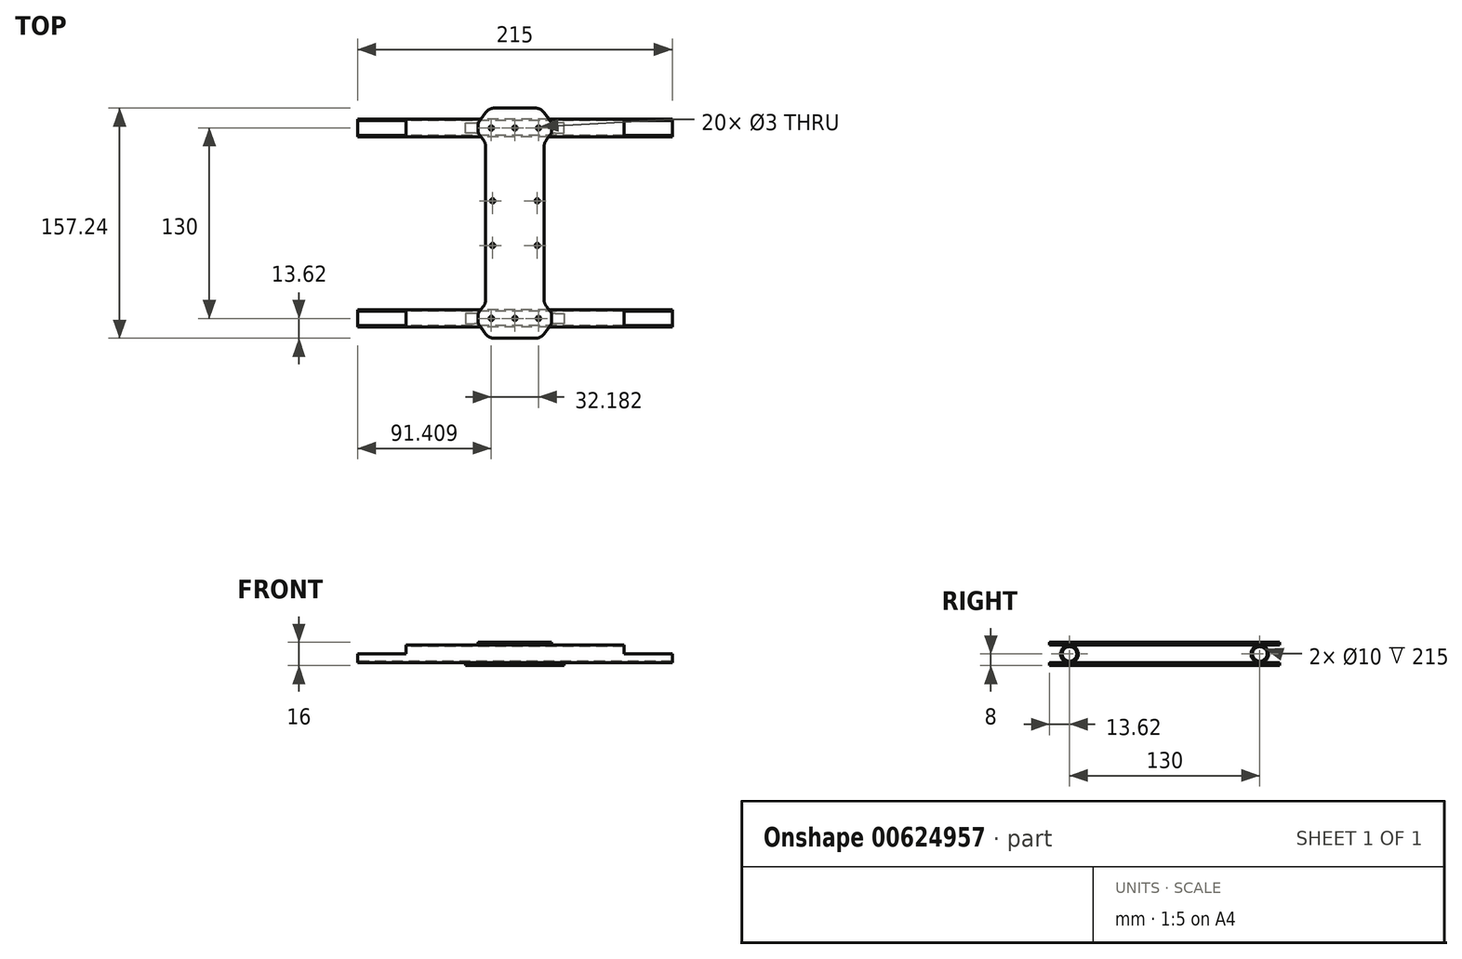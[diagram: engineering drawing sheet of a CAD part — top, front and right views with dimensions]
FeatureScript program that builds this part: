
annotation { "Feature Type Name" : "Feature", "Feature Type Description" : "" }
export const myFeature = defineFeature(function(context is Context, id is Id, definition is map)
    precondition{}
    {
        {
            var Q0;
            Q0=qCreatedBy(makeId("Top.planeOp"),FACE);
            var sketch = newSketch(context, id + "F0", { "sketchPlane" : qUnion([Q0])});
            skLineSegment(sketch, "E0.bottom", {"start": v(-20, 65) * mm, "end": v(20, 65) * mm, "construction": true});
            skLineSegment(sketch, "E0.top", {"start": v(-20, -65) * mm, "end": v(20, -65) * mm, "construction": true});
            skLineSegment(sketch, "E0.left", {"start": v(-20, 65) * mm, "end": v(-20, -65) * mm, "construction": true});
            skLineSegment(sketch, "E0.right", {"start": v(20, 65) * mm, "end": v(20, -65) * mm, "construction": true});
            skPoint(sketch, "E0.middle", {"position": v(0, 0) * mm});
            skSolve(sketch);
        }
        {
            var Q0;
            Q0=qCreatedBy(makeId("Right.planeOp"),FACE);
            var sketch = newSketch(context, id + "F1", { "sketchPlane" : qUnion([Q0])});
            skCircle(sketch, "E1", {"center": v(-65, 0) * mm, "radius": 6 * mm});
            skLineSegment(sketch, "E2", {"start": v(-65, 0) * mm, "end": v(0, 0) * mm, "construction": true});
            skLineSegment(sketch, "E3", {"start": v(0, 0) * mm, "end": v(64.7, 0) * mm, "construction": true});
            skLineSegment(sketch, "E4", {"start": v(0, 0) * mm, "end": v(0, 7.86) * mm, "construction": true});
            skCircle(sketch, "E5.MirrorC", {"center": v(65, 0) * mm, "radius": 6 * mm});
            skCircle(sketch, "E6", {"center": v(-65, 0) * mm, "radius": 5 * mm});
            skCircle(sketch, "E7.MirrorC", {"center": v(65, 0) * mm, "radius": 5 * mm});
            skSolve(sketch);
        }
        {
            var Q0;
            Q0 = qSketchRegion(id + "F1", true);
            extrude(context, id + "F2", {"entities" : qUnion([Q0]), "endBound" : BoundingType.SYMMETRIC, "depth" : 215 * mm, "offsetDistance" : 25 * mm});
        }
        {
            var Q0;
            Q0=qCreatedBy(makeId("Top.planeOp"),FACE);
            var sketch = newSketch(context, id + "F3", { "sketchPlane" : qUnion([Q0])});
            skLineSegment(sketch, "E8", {"start": v(-20, -54.92) * mm, "end": v(-25.19, -61.5) * mm});
            skLineSegment(sketch, "E9", {"start": v(-25.19, -61.5) * mm, "end": v(-33.69, -61.5) * mm});
            skLineSegment(sketch, "E10", {"start": v(-33.69, -61.5) * mm, "end": v(-33.62, -68.5) * mm});
            skLineSegment(sketch, "E11", {"start": v(-33.62, -68.5) * mm, "end": v(-25.12, -68.5) * mm});
            skLineSegment(sketch, "E12", {"start": v(-20, -54.92) * mm, "end": v(-20, 0) * mm});
            skLineSegment(sketch, "E13", {"start": v(-20, 0) * mm, "end": v(0, 0) * mm, "construction": true});
            skLineSegment(sketch, "E14", {"start": v(0, -75.74) * mm, "end": v(0, 0) * mm, "construction": true});
            skLineSegment(sketch, "E15", {"start": v(-25.12, -68.5) * mm, "end": v(-17.75, -78.62) * mm});
            skLineSegment(sketch, "E16", {"start": v(-17.75, -78.62) * mm, "end": v(0, -78.62) * mm});
            skLineSegment(sketch, "E17.MirrorCS", {"start": v(25.12, -68.5) * mm, "end": v(17.75, -78.62) * mm});
            skLineSegment(sketch, "E18.MirrorCS", {"start": v(25.19, -61.5) * mm, "end": v(33.69, -61.5) * mm});
            skLineSegment(sketch, "E19.MirrorCS", {"start": v(33.69, -61.5) * mm, "end": v(33.62, -68.5) * mm});
            skLineSegment(sketch, "E20.MirrorCS", {"start": v(20, 0) * mm, "end": v(0, 0) * mm, "construction": true});
            skLineSegment(sketch, "E21.MirrorCS", {"start": v(20, -54.92) * mm, "end": v(25.19, -61.5) * mm});
            skLineSegment(sketch, "E22.MirrorCS", {"start": v(20, -54.92) * mm, "end": v(20, 0) * mm});
            skLineSegment(sketch, "E23.MirrorCS", {"start": v(17.75, -78.62) * mm, "end": v(0, -78.62) * mm});
            skLineSegment(sketch, "E24.MirrorCS", {"start": v(33.62, -68.5) * mm, "end": v(25.12, -68.5) * mm});
            skLineSegment(sketch, "E25.MirrorCS", {"start": v(33.69, 61.5) * mm, "end": v(33.62, 68.5) * mm});
            skLineSegment(sketch, "E26.MirrorCS", {"start": v(-33.62, 68.5) * mm, "end": v(-25.12, 68.5) * mm});
            skLineSegment(sketch, "E27.MirrorCS", {"start": v(-33.69, 61.5) * mm, "end": v(-33.62, 68.5) * mm});
            skLineSegment(sketch, "E28.MirrorCS", {"start": v(17.75, 78.62) * mm, "end": v(0, 78.62) * mm});
            skLineSegment(sketch, "E29.MirrorCS", {"start": v(-20, 54.92) * mm, "end": v(-20, 0) * mm});
            skLineSegment(sketch, "E30.MirrorCS", {"start": v(-20, 54.92) * mm, "end": v(-25.19, 61.5) * mm});
            skLineSegment(sketch, "E31.MirrorCS", {"start": v(-17.75, 78.62) * mm, "end": v(0, 78.62) * mm});
            skLineSegment(sketch, "E32.MirrorCS", {"start": v(20, 54.92) * mm, "end": v(20, 0) * mm});
            skLineSegment(sketch, "E33.MirrorCS", {"start": v(-25.19, 61.5) * mm, "end": v(-33.69, 61.5) * mm});
            skLineSegment(sketch, "E34.MirrorCS", {"start": v(25.12, 68.5) * mm, "end": v(17.75, 78.62) * mm});
            skLineSegment(sketch, "E35.MirrorCS", {"start": v(20, 54.92) * mm, "end": v(25.19, 61.5) * mm});
            skLineSegment(sketch, "E36.MirrorCS", {"start": v(25.19, 61.5) * mm, "end": v(33.69, 61.5) * mm});
            skLineSegment(sketch, "E37.MirrorCS", {"start": v(-25.12, 68.5) * mm, "end": v(-17.75, 78.62) * mm});
            skLineSegment(sketch, "E38.MirrorCS", {"start": v(33.62, 68.5) * mm, "end": v(25.12, 68.5) * mm});
            skLineSegment(sketch, "E39.MirrorCS", {"start": v(0, 75.74) * mm, "end": v(0, 0) * mm, "construction": true});
            skLineSegment(sketch, "E40", {"start": v(0, -65) * mm, "end": v(-33.65, -65) * mm, "construction": true});
            skCircle(sketch, "E41", {"center": v(-16.1, -65) * mm, "radius": 1.5 * mm});
            skCircle(sketch, "E42.MirrorC", {"center": v(16.1, -65) * mm, "radius": 1.5 * mm});
            skCircle(sketch, "E43.MirrorC", {"center": v(16.1, 65) * mm, "radius": 1.5 * mm});
            skCircle(sketch, "E44.MirrorC", {"center": v(-16.1, 65) * mm, "radius": 1.5 * mm});
            skCircle(sketch, "E45", {"center": v(0, -65) * mm, "radius": 1.5 * mm});
            skCircle(sketch, "E46.MirrorC", {"center": v(0, 65) * mm, "radius": 1.5 * mm});
            skPoint(sketch, "E47.middle", {"position": v(0, 0) * mm});
            skCircle(sketch, "E48", {"center": v(-15.25, 15.25) * mm, "radius": 1.5 * mm});
            skCircle(sketch, "E49.MirrorC", {"center": v(-15.25, -15.25) * mm, "radius": 1.5 * mm});
            skCircle(sketch, "E50.MirrorC", {"center": v(15.25, 15.25) * mm, "radius": 1.5 * mm});
            skCircle(sketch, "E51.MirrorC", {"center": v(15.25, -15.25) * mm, "radius": 1.5 * mm});
            skSolve(sketch);
        }
        {
            var Q0;
            Q0=makeQuery(id+"F3.imprint","IMPRINT",FACE,{"disambiguationData":[TD([[makeQuery(id+"F3.imprint","IMPRINT",EDGE,{"derivedFrom":sQuery(id+"F3.wireOp",EDGE,"E8")}),1.0]])]});
            extrude(context, id + "F4", {"entities" : qUnion([Q0]), "oppositeDirection" : true, "depth" : 8 * mm, "offsetDistance" : 25 * mm, "hasSecondDirection" : true, "secondDirectionOppositeDirection" : true, "secondDirectionDepth" : 6 * mm});
        }
        {
            var Q0;
            Q0=qCreatedBy(makeId("Top.planeOp"),FACE);
            var sketch = newSketch(context, id + "F5", { "sketchPlane" : qUnion([Q0])});
            skLineSegment(sketch, "E52", {"start": v(-20, -54.92) * mm, "end": v(-25.19, -61.5) * mm});
            skLineSegment(sketch, "E53", {"start": v(-20, -54.92) * mm, "end": v(-20, 0) * mm});
            skLineSegment(sketch, "E54", {"start": v(-20, 0) * mm, "end": v(0, 0) * mm, "construction": true});
            skLineSegment(sketch, "E55", {"start": v(0, -75.74) * mm, "end": v(0, 0) * mm, "construction": true});
            skLineSegment(sketch, "E56", {"start": v(-25.12, -68.5) * mm, "end": v(-17.75, -78.62) * mm});
            skLineSegment(sketch, "E57", {"start": v(-17.75, -78.62) * mm, "end": v(0, -78.62) * mm});
            skLineSegment(sketch, "E58.MirrorCS", {"start": v(25.12, -68.5) * mm, "end": v(17.75, -78.62) * mm});
            skLineSegment(sketch, "E59.MirrorCS", {"start": v(20, 0) * mm, "end": v(0, 0) * mm, "construction": true});
            skLineSegment(sketch, "E60.MirrorCS", {"start": v(20, -54.92) * mm, "end": v(25.19, -61.5) * mm});
            skLineSegment(sketch, "E61.MirrorCS", {"start": v(20, -54.92) * mm, "end": v(20, 0) * mm});
            skLineSegment(sketch, "E62.MirrorCS", {"start": v(17.75, -78.62) * mm, "end": v(0, -78.62) * mm});
            skLineSegment(sketch, "E63.MirrorCS", {"start": v(17.75, 78.62) * mm, "end": v(0, 78.62) * mm});
            skLineSegment(sketch, "E64.MirrorCS", {"start": v(-20, 54.92) * mm, "end": v(-20, 0) * mm});
            skLineSegment(sketch, "E65.MirrorCS", {"start": v(-20, 54.92) * mm, "end": v(-25.19, 61.5) * mm});
            skLineSegment(sketch, "E66.MirrorCS", {"start": v(-17.75, 78.62) * mm, "end": v(0, 78.62) * mm});
            skLineSegment(sketch, "E67.MirrorCS", {"start": v(20, 54.92) * mm, "end": v(20, 0) * mm});
            skLineSegment(sketch, "E68.MirrorCS", {"start": v(25.12, 68.5) * mm, "end": v(17.75, 78.62) * mm});
            skLineSegment(sketch, "E69.MirrorCS", {"start": v(20, 54.92) * mm, "end": v(25.19, 61.5) * mm});
            skLineSegment(sketch, "E70.MirrorCS", {"start": v(-25.12, 68.5) * mm, "end": v(-17.75, 78.62) * mm});
            skLineSegment(sketch, "E71.MirrorCS", {"start": v(0, 75.74) * mm, "end": v(0, 0) * mm, "construction": true});
            skCircle(sketch, "E72", {"center": v(-16.1, -65) * mm, "radius": 1.5 * mm});
            skCircle(sketch, "E73.MirrorC", {"center": v(16.1, -65) * mm, "radius": 1.5 * mm});
            skCircle(sketch, "E74.MirrorC", {"center": v(16.1, 65) * mm, "radius": 1.5 * mm});
            skCircle(sketch, "E75.MirrorC", {"center": v(-16.1, 65) * mm, "radius": 1.5 * mm});
            skCircle(sketch, "E76", {"center": v(0, -65) * mm, "radius": 1.5 * mm});
            skCircle(sketch, "E77.MirrorC", {"center": v(0, 65) * mm, "radius": 1.5 * mm});
            skLineSegment(sketch, "E78", {"start": v(25.12, -68.5) * mm, "end": v(25.19, -61.5) * mm});
            skLineSegment(sketch, "E79.MirrorCS", {"start": v(-25.12, -68.5) * mm, "end": v(-25.19, -61.5) * mm});
            skLineSegment(sketch, "E80", {"start": v(25.19, 61.5) * mm, "end": v(25.12, 68.5) * mm});
            skLineSegment(sketch, "E81", {"start": v(-25.19, 61.5) * mm, "end": v(-25.12, 68.5) * mm});
            skPoint(sketch, "E82.middle", {"position": v(0, 0) * mm});
            skCircle(sketch, "E83", {"center": v(-15.25, 15.25) * mm, "radius": 1.5 * mm});
            skCircle(sketch, "E84.MirrorC", {"center": v(15.25, 15.25) * mm, "radius": 1.5 * mm});
            skCircle(sketch, "E85.MirrorC", {"center": v(15.25, -15.25) * mm, "radius": 1.5 * mm});
            skCircle(sketch, "E86.MirrorC", {"center": v(-15.25, -15.25) * mm, "radius": 1.5 * mm});
            skSolve(sketch);
        }
        {
            var Q0;
            Q0 = qSketchRegion(id + "F5", true);
            extrude(context, id + "F6", {"entities" : qUnion([Q0]), "depth" : 8 * mm, "offsetDistance" : 25 * mm, "hasSecondDirection" : true, "secondDirectionOppositeDirection" : false, "secondDirectionDepth" : 6 * mm});
        }
        {
            var Q0;
            Q0=qCreatedBy(makeId("Top.planeOp"),FACE);
            var sketch = newSketch(context, id + "F7", { "sketchPlane" : qUnion([Q0])});
            skLineSegment(sketch, "E87", {"start": v(0, 0) * mm, "end": v(0, -65) * mm, "construction": true});
            skLineSegment(sketch, "E88", {"start": v(0, -65) * mm, "end": v(91, -65) * mm, "construction": true});
            skLineSegment(sketch, "E89", {"start": v(0, 0) * mm, "end": v(43.65, 0) * mm, "construction": true});
            skLineSegment(sketch, "E90.bottom", {"start": v(74.5, -59) * mm, "end": v(107.5, -59) * mm});
            skLineSegment(sketch, "E90.top", {"start": v(74.5, -71) * mm, "end": v(107.5, -71) * mm});
            skLineSegment(sketch, "E90.left", {"start": v(74.5, -59) * mm, "end": v(74.5, -71) * mm});
            skLineSegment(sketch, "E90.right", {"start": v(107.5, -59) * mm, "end": v(107.5, -71) * mm});
            skPoint(sketch, "E90.middle", {"position": v(91, -65) * mm});
            skLineSegment(sketch, "E91.MirrorCS", {"start": v(-74.5, -59) * mm, "end": v(-107.5, -59) * mm});
            skLineSegment(sketch, "E92.MirrorCS", {"start": v(-74.5, -59) * mm, "end": v(-74.5, -71) * mm});
            skLineSegment(sketch, "E93.MirrorCS", {"start": v(-74.5, -71) * mm, "end": v(-107.5, -71) * mm});
            skLineSegment(sketch, "E94.MirrorCS", {"start": v(-107.5, -59) * mm, "end": v(-107.5, -71) * mm});
            skPoint(sketch, "E95.MirrorP", {"position": v(-91, -65) * mm});
            skLineSegment(sketch, "E96.MirrorCS", {"start": v(107.5, 59) * mm, "end": v(107.5, 71) * mm});
            skLineSegment(sketch, "E97.MirrorCS", {"start": v(0, 65) * mm, "end": v(91, 65) * mm, "construction": true});
            skLineSegment(sketch, "E98.MirrorCS", {"start": v(-74.5, 59) * mm, "end": v(-74.5, 71) * mm});
            skLineSegment(sketch, "E99.MirrorCS", {"start": v(-107.5, 59) * mm, "end": v(-107.5, 71) * mm});
            skPoint(sketch, "E100.MirrorP", {"position": v(91, 65) * mm});
            skLineSegment(sketch, "E101.MirrorCS", {"start": v(-74.5, 59) * mm, "end": v(-107.5, 59) * mm});
            skPoint(sketch, "E102.MirrorP", {"position": v(-91, 65) * mm});
            skLineSegment(sketch, "E103.MirrorCS", {"start": v(74.5, 59) * mm, "end": v(74.5, 71) * mm});
            skLineSegment(sketch, "E104.MirrorCS", {"start": v(0, 0) * mm, "end": v(0, 65) * mm, "construction": true});
            skLineSegment(sketch, "E105.MirrorCS", {"start": v(-74.5, 71) * mm, "end": v(-107.5, 71) * mm});
            skLineSegment(sketch, "E106.MirrorCS", {"start": v(74.5, 71) * mm, "end": v(107.5, 71) * mm});
            skLineSegment(sketch, "E107.MirrorCS", {"start": v(74.5, 59) * mm, "end": v(107.5, 59) * mm});
            skSolve(sketch);
        }
        {
            var Q0;
            Q0 = qSketchRegion(id + "F7", true);
            extrude(context, id + "F8", {"entities" : qUnion([Q0]), "operationType" : NewBodyOperationType.REMOVE, "depth" : 6 * mm, "offsetDistance" : 25 * mm});
        }
        {
            var Q0;
            Q0=makeQuery(id+"F4.opExtrude","SWEPT_EDGE",EDGE,{"disambiguationData":[OSD([sQuery(id+"F3.wireOp",EDGE,"E11"),sQuery(id+"F3.wireOp",EDGE,"E15")])]});
            var Q1;
            Q1=makeQuery(id+"F4.opExtrude","SWEPT_EDGE",EDGE,{"disambiguationData":[OSD([sQuery(id+"F3.wireOp",EDGE,"E17.MirrorCS"),sQuery(id+"F3.wireOp",EDGE,"E24.MirrorCS")])]});
            var Q2;
            Q2=makeQuery(id+"F4.opExtrude","SWEPT_EDGE",EDGE,{"disambiguationData":[OSD([sQuery(id+"F3.wireOp",EDGE,"E18.MirrorCS"),sQuery(id+"F3.wireOp",EDGE,"E21.MirrorCS")])]});
            var Q3;
            Q3=makeQuery(id+"F4.opExtrude","SWEPT_EDGE",EDGE,{"disambiguationData":[OSD([sQuery(id+"F3.wireOp",EDGE,"E8"),sQuery(id+"F3.wireOp",EDGE,"E9")])]});
            var Q4;
            Q4=makeQuery(id+"F4.opExtrude","SWEPT_EDGE",EDGE,{"disambiguationData":[OSD([sQuery(id+"F3.wireOp",EDGE,"E26.MirrorCS"),sQuery(id+"F3.wireOp",EDGE,"E37.MirrorCS")])]});
            var Q5;
            Q5=makeQuery(id+"F4.opExtrude","SWEPT_EDGE",EDGE,{"disambiguationData":[OSD([sQuery(id+"F3.wireOp",EDGE,"E34.MirrorCS"),sQuery(id+"F3.wireOp",EDGE,"E38.MirrorCS")])]});
            var Q6;
            Q6=makeQuery(id+"F4.opExtrude","SWEPT_EDGE",EDGE,{"disambiguationData":[OSD([sQuery(id+"F3.wireOp",EDGE,"E35.MirrorCS"),sQuery(id+"F3.wireOp",EDGE,"E36.MirrorCS")])]});
            var Q7;
            Q7=makeQuery(id+"F4.opExtrude","SWEPT_EDGE",EDGE,{"disambiguationData":[OSD([sQuery(id+"F3.wireOp",EDGE,"E30.MirrorCS"),sQuery(id+"F3.wireOp",EDGE,"E33.MirrorCS")])]});
            var Q8;
            Q8=makeQuery(id+"F6.opExtrude","SWEPT_EDGE",EDGE,{"disambiguationData":[OSD([sQuery(id+"F5.wireOp",EDGE,"E70.MirrorCS"),sQuery(id+"F5.wireOp",EDGE,"E81")])]});
            var Q9;
            Q9=makeQuery(id+"F6.opExtrude","SWEPT_EDGE",EDGE,{"disambiguationData":[OSD([sQuery(id+"F5.wireOp",EDGE,"E65.MirrorCS"),sQuery(id+"F5.wireOp",EDGE,"E81")])]});
            var Q10;
            Q10=makeQuery(id+"F6.opExtrude","SWEPT_EDGE",EDGE,{"disambiguationData":[OSD([sQuery(id+"F5.wireOp",EDGE,"E68.MirrorCS"),sQuery(id+"F5.wireOp",EDGE,"E80")])]});
            var Q11;
            Q11=makeQuery(id+"F6.opExtrude","SWEPT_EDGE",EDGE,{"disambiguationData":[OSD([sQuery(id+"F5.wireOp",EDGE,"E69.MirrorCS"),sQuery(id+"F5.wireOp",EDGE,"E80")])]});
            var Q12;
            Q12=makeQuery(id+"F6.opExtrude","SWEPT_EDGE",EDGE,{"disambiguationData":[OSD([sQuery(id+"F5.wireOp",EDGE,"E58.MirrorCS"),sQuery(id+"F5.wireOp",EDGE,"E78")])]});
            var Q13;
            Q13=makeQuery(id+"F6.opExtrude","SWEPT_EDGE",EDGE,{"disambiguationData":[OSD([sQuery(id+"F5.wireOp",EDGE,"E60.MirrorCS"),sQuery(id+"F5.wireOp",EDGE,"E78")])]});
            var Q14;
            Q14=makeQuery(id+"F6.opExtrude","SWEPT_EDGE",EDGE,{"disambiguationData":[OSD([sQuery(id+"F5.wireOp",EDGE,"E52"),sQuery(id+"F5.wireOp",EDGE,"E79.MirrorCS")])]});
            var Q15;
            Q15=makeQuery(id+"F6.opExtrude","SWEPT_EDGE",EDGE,{"disambiguationData":[OSD([sQuery(id+"F5.wireOp",EDGE,"E56"),sQuery(id+"F5.wireOp",EDGE,"E79.MirrorCS")])]});
            var Q16;
            Q16=makeQuery(id+"FRUV5qcOZJ5jhgf_4.opExtrude","SWEPT_EDGE",EDGE,{"disambiguationData":[OSD([sQuery(id+"FPOVCmEpiKDNWGi_4.wireOp",EDGE,"b42ecf09-6dc6-4207-b51f-dcecceab576b.MirrorCS"),sQuery(id+"FPOVCmEpiKDNWGi_4.wireOp",EDGE,"35af5927-bb7d-4a19-8fb0-2eac8ffebaeb")])]});
            var Q17;
            Q17=makeQuery(id+"FRUV5qcOZJ5jhgf_4.opExtrude","SWEPT_EDGE",EDGE,{"disambiguationData":[OSD([sQuery(id+"FPOVCmEpiKDNWGi_4.wireOp",EDGE,"97de2fec-c19a-4408-b6b3-02fe6345d77e.MirrorCS"),sQuery(id+"FPOVCmEpiKDNWGi_4.wireOp",EDGE,"35af5927-bb7d-4a19-8fb0-2eac8ffebaeb")])]});
            var Q18;
            Q18=makeQuery(id+"FRUV5qcOZJ5jhgf_4.opExtrude","SWEPT_EDGE",EDGE,{"disambiguationData":[OSD([sQuery(id+"FPOVCmEpiKDNWGi_4.wireOp",EDGE,"46e9c258-9e58-4d26-8021-a2ccb4e2b974.MirrorCS"),sQuery(id+"FPOVCmEpiKDNWGi_4.wireOp",EDGE,"e85c2889-23f9-49fd-8fc6-b68ef9be6dd2")])]});
            var Q19;
            Q19=makeQuery(id+"FRUV5qcOZJ5jhgf_4.opExtrude","SWEPT_EDGE",EDGE,{"disambiguationData":[OSD([sQuery(id+"FPOVCmEpiKDNWGi_4.wireOp",EDGE,"b1dd11ee-b3e0-4977-90c2-f60ee6d27586.MirrorCS"),sQuery(id+"FPOVCmEpiKDNWGi_4.wireOp",EDGE,"e85c2889-23f9-49fd-8fc6-b68ef9be6dd2")])]});
            var Q20;
            Q20=makeQuery(id+"FRUV5qcOZJ5jhgf_4.opExtrude","SWEPT_EDGE",EDGE,{"disambiguationData":[OSD([sQuery(id+"FPOVCmEpiKDNWGi_4.wireOp",EDGE,"41c56124-091f-4bfc-87e4-0effb01823fb.MirrorCS"),sQuery(id+"FPOVCmEpiKDNWGi_4.wireOp",EDGE,"41155186-b6f0-42d8-86f9-b8dc6bf684e1")])]});
            var Q21;
            Q21=makeQuery(id+"FRUV5qcOZJ5jhgf_4.opExtrude","SWEPT_EDGE",EDGE,{"disambiguationData":[OSD([sQuery(id+"FPOVCmEpiKDNWGi_4.wireOp",EDGE,"9b6425d3-5aca-4adc-8dc5-8d42905c519e.MirrorCS"),sQuery(id+"FPOVCmEpiKDNWGi_4.wireOp",EDGE,"41155186-b6f0-42d8-86f9-b8dc6bf684e1")])]});
            var Q22;
            Q22=makeQuery(id+"FRUV5qcOZJ5jhgf_4.opExtrude","SWEPT_EDGE",EDGE,{"disambiguationData":[OSD([sQuery(id+"FPOVCmEpiKDNWGi_4.wireOp",EDGE,"9a405053-cc7c-4e3b-ba71-51e772f208f1"),sQuery(id+"FPOVCmEpiKDNWGi_4.wireOp",EDGE,"5861f194-80c3-4196-93a7-092f7c520be6.MirrorCS")])]});
            fillet(context, id + "F9", {"entities" : qUnion([Q0, Q1, Q2, Q3, Q4, Q5, Q6, Q7, Q8, Q9, Q10, Q11, Q12, Q13, Q14, Q15, Q16, Q17, Q18, Q19, Q20, Q21, Q22]), "radius" : 5 * mm, "tangentPropagation" : true, "allowEdgeOverflow" : false});
        }
        {
            var Q0;
            Q0=makeQuery(id+"F4.opExtrude","SWEPT_EDGE",EDGE,{"disambiguationData":[OSD([sQuery(id+"F3.wireOp",EDGE,"E28.MirrorCS"),sQuery(id+"F3.wireOp",EDGE,"E34.MirrorCS")])]});
            var Q1;
            Q1=makeQuery(id+"F4.opExtrude","SWEPT_EDGE",EDGE,{"disambiguationData":[OSD([sQuery(id+"F3.wireOp",EDGE,"E31.MirrorCS"),sQuery(id+"F3.wireOp",EDGE,"E37.MirrorCS")])]});
            var Q2;
            Q2=makeQuery(id+"F4.opExtrude","SWEPT_EDGE",EDGE,{"disambiguationData":[OSD([sQuery(id+"F3.wireOp",EDGE,"E29.MirrorCS"),sQuery(id+"F3.wireOp",EDGE,"E30.MirrorCS")])]});
            var Q3;
            Q3=makeQuery(id+"F4.opExtrude","SWEPT_EDGE",EDGE,{"disambiguationData":[OSD([sQuery(id+"F3.wireOp",EDGE,"E32.MirrorCS"),sQuery(id+"F3.wireOp",EDGE,"E35.MirrorCS")])]});
            var Q4;
            Q4=makeQuery(id+"F4.opExtrude","SWEPT_EDGE",EDGE,{"disambiguationData":[OSD([sQuery(id+"F3.wireOp",EDGE,"E21.MirrorCS"),sQuery(id+"F3.wireOp",EDGE,"E22.MirrorCS")])]});
            var Q5;
            Q5=makeQuery(id+"F4.opExtrude","SWEPT_EDGE",EDGE,{"disambiguationData":[OSD([sQuery(id+"F3.wireOp",EDGE,"E17.MirrorCS"),sQuery(id+"F3.wireOp",EDGE,"E23.MirrorCS")])]});
            var Q6;
            Q6=makeQuery(id+"F4.opExtrude","SWEPT_EDGE",EDGE,{"disambiguationData":[OSD([sQuery(id+"F3.wireOp",EDGE,"E15"),sQuery(id+"F3.wireOp",EDGE,"E16")])]});
            var Q7;
            Q7=makeQuery(id+"F4.opExtrude","SWEPT_EDGE",EDGE,{"disambiguationData":[OSD([sQuery(id+"F3.wireOp",EDGE,"E8"),sQuery(id+"F3.wireOp",EDGE,"E12")])]});
            var Q8;
            Q8=makeQuery(id+"F6.opExtrude","SWEPT_EDGE",EDGE,{"disambiguationData":[OSD([sQuery(id+"F5.wireOp",EDGE,"E66.MirrorCS"),sQuery(id+"F5.wireOp",EDGE,"E70.MirrorCS")])]});
            var Q9;
            Q9=makeQuery(id+"F6.opExtrude","SWEPT_EDGE",EDGE,{"disambiguationData":[OSD([sQuery(id+"F5.wireOp",EDGE,"E63.MirrorCS"),sQuery(id+"F5.wireOp",EDGE,"E68.MirrorCS")])]});
            var Q10;
            Q10=makeQuery(id+"F6.opExtrude","SWEPT_EDGE",EDGE,{"disambiguationData":[OSD([sQuery(id+"F5.wireOp",EDGE,"E60.MirrorCS"),sQuery(id+"F5.wireOp",EDGE,"E61.MirrorCS")])]});
            var Q11;
            Q11=makeQuery(id+"F6.opExtrude","SWEPT_EDGE",EDGE,{"disambiguationData":[OSD([sQuery(id+"F5.wireOp",EDGE,"E67.MirrorCS"),sQuery(id+"F5.wireOp",EDGE,"E69.MirrorCS")])]});
            var Q12;
            Q12=makeQuery(id+"F6.opExtrude","SWEPT_EDGE",EDGE,{"disambiguationData":[OSD([sQuery(id+"F5.wireOp",EDGE,"E58.MirrorCS"),sQuery(id+"F5.wireOp",EDGE,"E62.MirrorCS")])]});
            var Q13;
            Q13=makeQuery(id+"F6.opExtrude","SWEPT_EDGE",EDGE,{"disambiguationData":[OSD([sQuery(id+"F5.wireOp",EDGE,"E56"),sQuery(id+"F5.wireOp",EDGE,"E57")])]});
            var Q14;
            Q14=makeQuery(id+"F6.opExtrude","SWEPT_EDGE",EDGE,{"disambiguationData":[OSD([sQuery(id+"F5.wireOp",EDGE,"E52"),sQuery(id+"F5.wireOp",EDGE,"E53")])]});
            var Q15;
            Q15=makeQuery(id+"F6.opExtrude","SWEPT_EDGE",EDGE,{"disambiguationData":[OSD([sQuery(id+"F5.wireOp",EDGE,"E64.MirrorCS"),sQuery(id+"F5.wireOp",EDGE,"E65.MirrorCS")])]});
            var Q16;
            Q16=makeQuery(id+"FRUV5qcOZJ5jhgf_4.opExtrude","SWEPT_EDGE",EDGE,{"disambiguationData":[OSD([sQuery(id+"FPOVCmEpiKDNWGi_4.wireOp",EDGE,"97de2fec-c19a-4408-b6b3-02fe6345d77e.MirrorCS"),sQuery(id+"FPOVCmEpiKDNWGi_4.wireOp",EDGE,"95c3b9ba-4883-4b31-b5ee-f706eb17b36c.MirrorCS")])]});
            var Q17;
            Q17=makeQuery(id+"FRUV5qcOZJ5jhgf_4.opExtrude","SWEPT_EDGE",EDGE,{"disambiguationData":[OSD([sQuery(id+"FPOVCmEpiKDNWGi_4.wireOp",EDGE,"20a90ce0-b235-4bf8-94c6-5e64ed045909.MirrorCS"),sQuery(id+"FPOVCmEpiKDNWGi_4.wireOp",EDGE,"46e9c258-9e58-4d26-8021-a2ccb4e2b974.MirrorCS")])]});
            var Q18;
            Q18=makeQuery(id+"FRUV5qcOZJ5jhgf_4.opExtrude","SWEPT_EDGE",EDGE,{"disambiguationData":[OSD([sQuery(id+"FPOVCmEpiKDNWGi_4.wireOp",EDGE,"7ea5ebd3-14a3-4d2b-b51a-3041f3b1c881"),sQuery(id+"FPOVCmEpiKDNWGi_4.wireOp",EDGE,"1a579a42-bdaa-4e9a-8b4e-0b3a97781a8c")])]});
            var Q19;
            Q19=makeQuery(id+"FRUV5qcOZJ5jhgf_4.opExtrude","SWEPT_EDGE",EDGE,{"disambiguationData":[OSD([sQuery(id+"FPOVCmEpiKDNWGi_4.wireOp",EDGE,"4f184554-60bf-4eba-95c6-cc1606bdb317.MirrorCS"),sQuery(id+"FPOVCmEpiKDNWGi_4.wireOp",EDGE,"9b6425d3-5aca-4adc-8dc5-8d42905c519e.MirrorCS")])]});
            var Q20;
            Q20=makeQuery(id+"FRUV5qcOZJ5jhgf_4.opExtrude","SWEPT_EDGE",EDGE,{"disambiguationData":[OSD([sQuery(id+"FPOVCmEpiKDNWGi_4.wireOp",EDGE,"9a405053-cc7c-4e3b-ba71-51e772f208f1"),sQuery(id+"FPOVCmEpiKDNWGi_4.wireOp",EDGE,"b1733112-acb0-4289-8b6a-faea72016fe8")])]});
            var Q21;
            Q21=makeQuery(id+"FRUV5qcOZJ5jhgf_4.opExtrude","SWEPT_EDGE",EDGE,{"disambiguationData":[OSD([sQuery(id+"FPOVCmEpiKDNWGi_4.wireOp",EDGE,"db871104-896a-4074-963b-3f9e83e128f8.MirrorCS"),sQuery(id+"FPOVCmEpiKDNWGi_4.wireOp",EDGE,"41c56124-091f-4bfc-87e4-0effb01823fb.MirrorCS")])]});
            var Q22;
            Q22=makeQuery(id+"FRUV5qcOZJ5jhgf_4.opExtrude","SWEPT_EDGE",EDGE,{"disambiguationData":[OSD([sQuery(id+"FPOVCmEpiKDNWGi_4.wireOp",EDGE,"b42ecf09-6dc6-4207-b51f-dcecceab576b.MirrorCS"),sQuery(id+"FPOVCmEpiKDNWGi_4.wireOp",EDGE,"72427715-28a6-4ee9-8315-828bc08fcbf3.MirrorCS")])]});
            fillet(context, id + "F10", {"entities" : qUnion([Q0, Q1, Q2, Q3, Q4, Q5, Q6, Q7, Q8, Q9, Q10, Q11, Q12, Q13, Q14, Q15, Q16, Q17, Q18, Q19, Q20, Q21, Q22]), "radius" : 7.46 * mm, "tangentPropagation" : true, "allowEdgeOverflow" : false});
        }
    });
